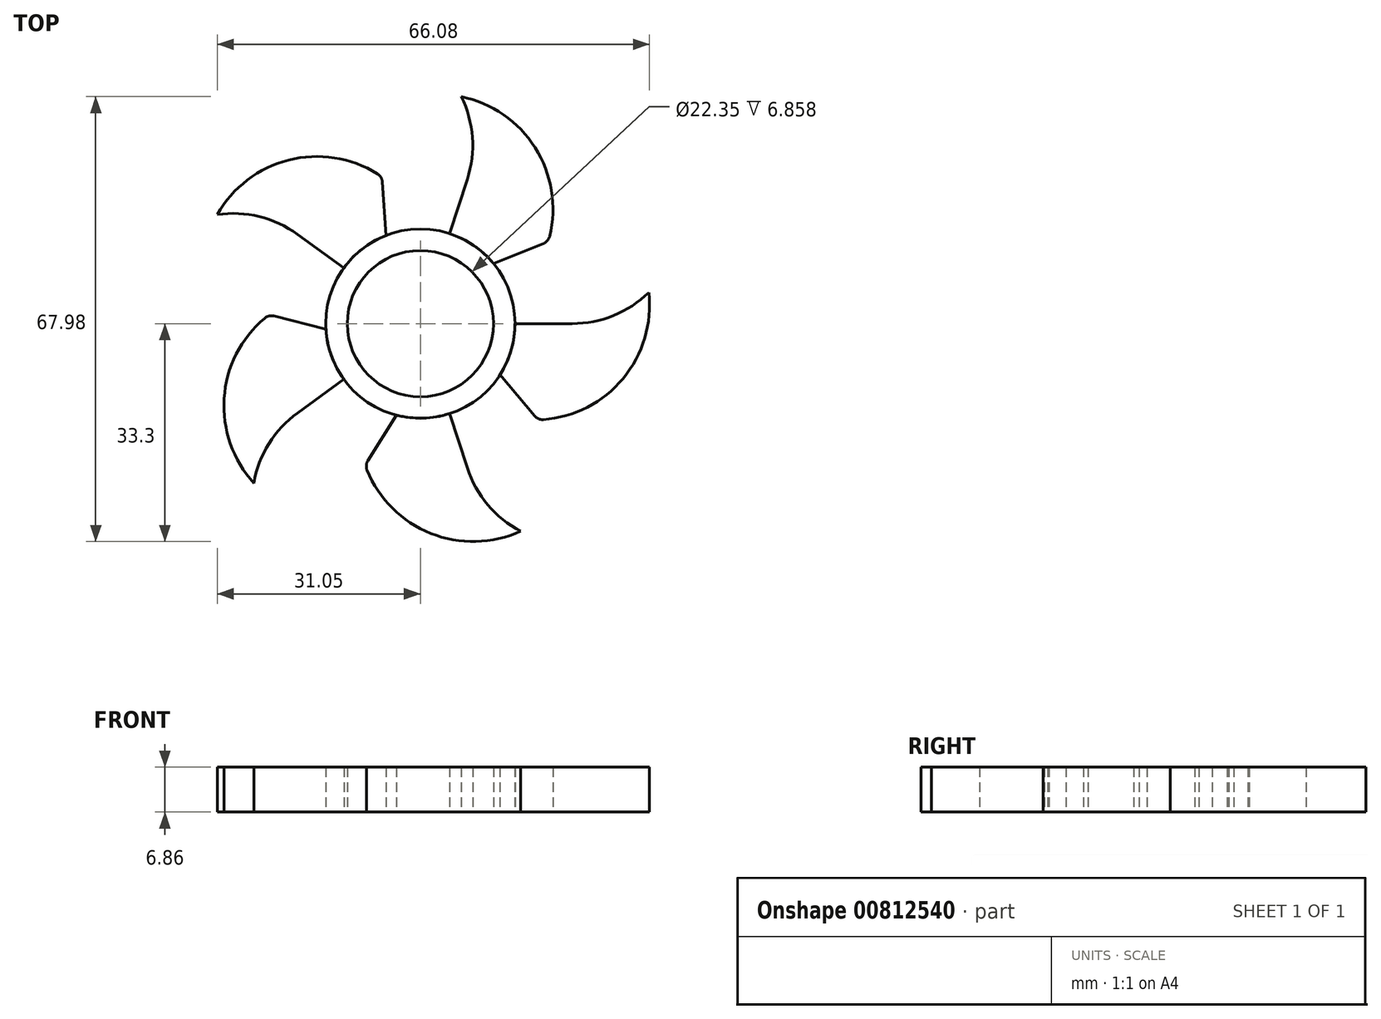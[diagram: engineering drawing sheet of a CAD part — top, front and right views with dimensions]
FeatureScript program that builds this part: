
annotation { "Feature Type Name" : "Feature", "Feature Type Description" : "" }
export const myFeature = defineFeature(function(context is Context, id is Id, definition is map)
    precondition{}
    {
        {
            var Q0;
            Q0=qCreatedBy(makeId("Top.planeOp"),FACE);
            var sketch = newSketch(context, id + "F0", { "sketchPlane" : qUnion([Q0])});
            skCircle(sketch, "E0", {"center": v(0, 0) * mm, "radius": 35.24 * mm});
            skCircle(sketch, "E1", {"center": v(0, 0) * mm, "radius": 23.22 * mm});
            skCircle(sketch, "E2", {"center": v(0, 0) * mm, "radius": 11.18 * mm});
            skCircle(sketch, "E3", {"center": v(0, 0) * mm, "radius": 14.48 * mm});
            skSolve(sketch);
        }
        {
            var Q0;
            Q0=makeQuery(id+"F0.imprint","IMPRINT",FACE,{"disambiguationData":[TD([[makeQuery(id+"F0.imprint","IMPRINT",EDGE,{"derivedFrom":sQuery(id+"F0.wireOp",EDGE,"E2")}),-1.0]])]});
            extrude(context, id + "F1", {"entities" : qUnion([Q0]), "endBound" : BoundingType.SYMMETRIC, "depth" : 6.86 * mm, "offsetDistance" : 25.4 * mm});
        }
        {
            var Q0;
            Q0=qCreatedBy(makeId("Top.planeOp"),FACE);
            var sketch = newSketch(context, id + "F2", { "sketchPlane" : qUnion([Q0])});
            skLineSegment(sketch, "E4", {"start": v(14.45, 0) * mm, "end": v(23.22, 0) * mm});
            skArc(sketch, "E5", {"start": v(23.22, 0) * mm, "mid": v(29.53, 1.24) * mm, "end": v(34.92, 4.76) * mm});
            skArc(sketch, "E6", {"start": v(17.96, -14.7) * mm, "mid": v(30.72, -8.7) * mm, "end": v(34.92, 4.76) * mm});
            skLineSegment(sketch, "E7", {"start": v(17.96, -14.7) * mm, "end": v(12.16, -7.8) * mm});
            skArc(sketch, "E8", {"start": v(12.16, -7.8) * mm, "mid": v(13.87, -4.07) * mm, "end": v(14.45, 0) * mm});
            skSolve(sketch);
        }
        {
            var Q0;
            Q0 = qSketchRegion(id + "F2", true);
            extrude(context, id + "F3", {"entities" : qUnion([Q0]), "endBound" : BoundingType.SYMMETRIC, "depth" : 6.86 * mm, "offsetDistance" : 25.4 * mm});
        }
        {
            var Q0;
            Q0=makeQuery(id+"F3.opExtrude","SWEPT_EDGE",EDGE,{"disambiguationData":[OSD([sQuery(id+"F2.wireOp",EDGE,"E6"),sQuery(id+"F2.wireOp",EDGE,"E7")])]});
            fillet(context, id + "F4", {"entities" : qUnion([Q0]), "radius" : 1.59 * mm, "tangentPropagation" : true, "allowEdgeOverflow" : false});
        }
        {
            var Q0;
            Q0=makeQuery(id+"F3.opExtrude","SWEPT_BODY",BODY,{"disambiguationData":[OSD([sQuery(id+"F2.wireOp",EDGE,"E4"),sQuery(id+"F2.wireOp",EDGE,"E5"),sQuery(id+"F2.wireOp",EDGE,"E6"),sQuery(id+"F2.wireOp",EDGE,"E7"),sQuery(id+"F2.wireOp",EDGE,"E8")])]});
            var Q1;
            Q1=sQuery(id+"F0.wireOp",EDGE,"E3");
            circularPattern(context, id + "F5", {"entities" : qUnion([Q0]), "axis" : qUnion([Q1]), "angle" : 360 * degree, "instanceCount" : 5, "oppositeDirection" : true, "equalSpace" : true});
        }
    });
